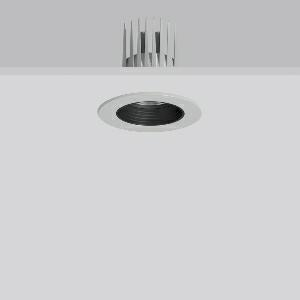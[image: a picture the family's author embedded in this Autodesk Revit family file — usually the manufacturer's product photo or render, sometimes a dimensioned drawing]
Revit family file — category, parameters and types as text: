
# Revit family: heledon_mini_e_901752_004_2_c6da
name_source: partatom
category: Lighting Fixtures
units: mm (PartAtom-declared; Revit-internal decimal feet)

## family parameters
Cut with Voids When Loaded = No
Host = Face
Light Source = No
Part Type = Normal
Room Calculation Point = No
Round Connector Dimension = Use Diameter
Shared = No

## types (1)
- HELEDON mini E (1 x LED Modul 927, 2850 lm, 2700)
    Apparent Load = 29 VA
    Approval mark = CE
    CIE Flux Codes = 96 100 100 100 100
    Color Rendering = 92
    Color Temperature = 2700
    Default Elevation = 1800 mm
    Description = Series: HELEDON mini
Round recessed downlight. Housing: die-cast aluminium, powder-coated. Black plastic ring and recessed LED to prevent glare from the side. Optical assembly with lens made of plastic (polycarbonate) for the best homogeneous light distribution - can be changed without tools. Best colour rendering index Ra>90. Suitable for Recessed ceiling mounting. Installation without tools thanks to spring fastening system. Including separate LED converter with connecting cable 600 mm.High quality converter without flickering and stroboscopic effect. Through-wiring box (5 pole) available as accessory. The following accessories can be mounted without use of tools: interchangeable lenses, decorative glasses, honeycomb louvre, clear and frosted diffusers, white interchangeable plastic ring. 
Colour: silver
Diameter: 124 mm
Height: 3 mm
Cut-out diameter: 114 mm
Recess height: 170 mm
Luminaire: recess height: 120 mm
Lamp: LED
Socket: without socket
Colour temperature: 2700K
Colour rendering index (CRI): 92
System power: 29 W
Rated luminous flux: 2850 lm
Luminous efficiency: 98 lm/W
Control gear: Regulated power supply
Protection class: II
Type of protection: IP 20
    Height = 0 mm  [stored 0 ft]
    Lamp = 1 x LED Modul 927
    Lamp Light Flux = 2850 lm
    Lamp count = 1
    Length = 124 mm  [stored 0.406824 ft]
    Lifetime = 50000 h
    Luminous efficacy = 98 lm/W
    Manufacturer = RZB
    ModVariant = No
    Model = 901752.004.2
    Mounting Place = Ceiling
    Mounting Type = Recessed
    Number of Poles = 1
    OnlyDefault = Yes
    Power Factor = 1
    Product Name = HELEDON mini E
    Product group = Recessed downlights
    ProductGroupID = 402
    Protection Class = Protection class II
    Protection Degree = IP 20
    RLX_Detail_Level = 1
    RLX_Emergency_Light_Flux = 0 lm
    RLX_Emergency_Type = 0
    RLX_Emergency_Type_DB = No
    RlxData = <blob elided: 128277 chars, md5=39408b0b>
    Socket = socket
    Standby Power = 0 W
    System Light Flux = 2850 lm
    System Power = 29 W
    Type Comments = Product without accessories
    Type Image = 901656.004.jpg
    URL = http://relux.com
    VarID = ---
    Voltage = 230 V
    Voltage Range = 220-240 V
    Weight = 0.00 kg
    Width = 0 mm  [stored 0 ft]

note: [stored X ft] marks values corroborated as IEEE doubles in the binary element streams (Revit-internal decimal feet)

## geometry (parser evidence)
native form markers: Blend x4, Sweep x12
no freeform markers — native parametric forms only
